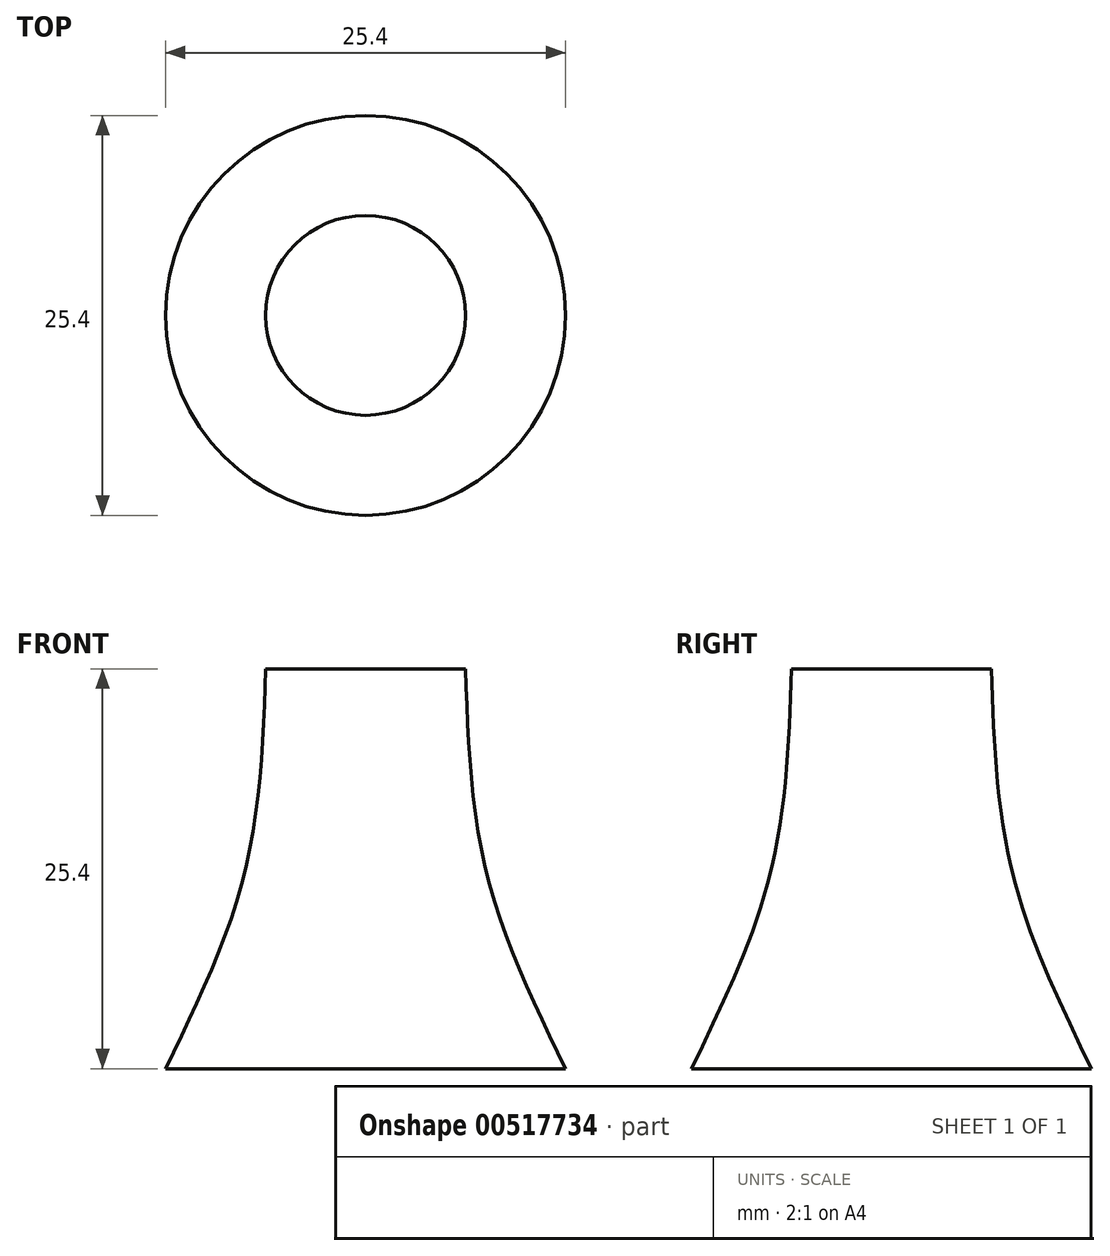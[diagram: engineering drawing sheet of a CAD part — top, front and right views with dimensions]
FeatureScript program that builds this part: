
annotation { "Feature Type Name" : "Feature", "Feature Type Description" : "" }
export const myFeature = defineFeature(function(context is Context, id is Id, definition is map)
    precondition{}
    {
        {
            var Q0;
            Q0=qCreatedBy(makeId("Top.planeOp"),FACE);
            var sketch = newSketch(context, id + "F0", { "sketchPlane" : qUnion([Q0])});
            skCircle(sketch, "E0", {"center": v(0, 0) * mm, "radius": 12.7 * mm});
            skSolve(sketch);
        }
        {
            var Q0;
            Q0=qCreatedBy(makeId("Top.planeOp"),FACE);
            cPlane(context, id + "F1", {"entities" : qUnion([Q0]), "cplaneType" : CPlaneType.OFFSET, "offset" : 25.4 * mm, "width" : 152.4 * mm, "height" : 152.4 * mm});
        }
        {
            var Q0;
            Q0=qCreatedBy(id+"F1.planeOp",FACE);
            var sketch = newSketch(context, id + "F2", { "sketchPlane" : qUnion([Q0])});
            skCircle(sketch, "E1", {"center": v(0, 0) * mm, "radius": 6.35 * mm});
            skSolve(sketch);
        }
        {
            var Q0;
            Q0=makeQuery(id+"F0.imprint","IMPRINT",FACE,{"disambiguationData":[TD([[makeQuery(id+"F0.imprint","IMPRINT",EDGE,{"derivedFrom":sQuery(id+"F0.wireOp",EDGE,"E0")}),1.0]])]});
            cPlane(context, id + "F3", {"entities" : qUnion([Q0]), "cplaneType" : CPlaneType.OFFSET, "offset" : 12.7 * mm, "width" : 152.4 * mm, "height" : 152.4 * mm});
        }
        {
            var Q0;
            Q0=qCreatedBy(id+"F3.planeOp",FACE);
            var sketch = newSketch(context, id + "F4", { "sketchPlane" : qUnion([Q0])});
            skCircle(sketch, "E2", {"center": v(0, 0) * mm, "radius": 7.62 * mm});
            skSolve(sketch);
        }
        {
            var Q0;
            Q0=makeQuery(id+"F0.imprint","IMPRINT",FACE,{"disambiguationData":[TD([[makeQuery(id+"F0.imprint","IMPRINT",EDGE,{"derivedFrom":sQuery(id+"F0.wireOp",EDGE,"E0")}),1.0]])]});
            var Q1;
            Q1=makeQuery(id+"F4.imprint","IMPRINT",FACE,{"disambiguationData":[TD([[makeQuery(id+"F4.imprint","IMPRINT",EDGE,{"derivedFrom":sQuery(id+"F4.wireOp",EDGE,"E2")}),1.0]])]});
            var Q2;
            Q2=makeQuery(id+"F2.imprint","IMPRINT",FACE,{"disambiguationData":[TD([[makeQuery(id+"F2.imprint","IMPRINT",EDGE,{"derivedFrom":sQuery(id+"F2.wireOp",EDGE,"E1")}),1.0]])]});
            loft(context, id + "F5", {"sheetProfilesArray" : [{ "sheetProfileEntities" : qUnion([Q0]) }, { "sheetProfileEntities" : qUnion([Q1]) }, { "sheetProfileEntities" : qUnion([Q2]) }]});
        }
    });
